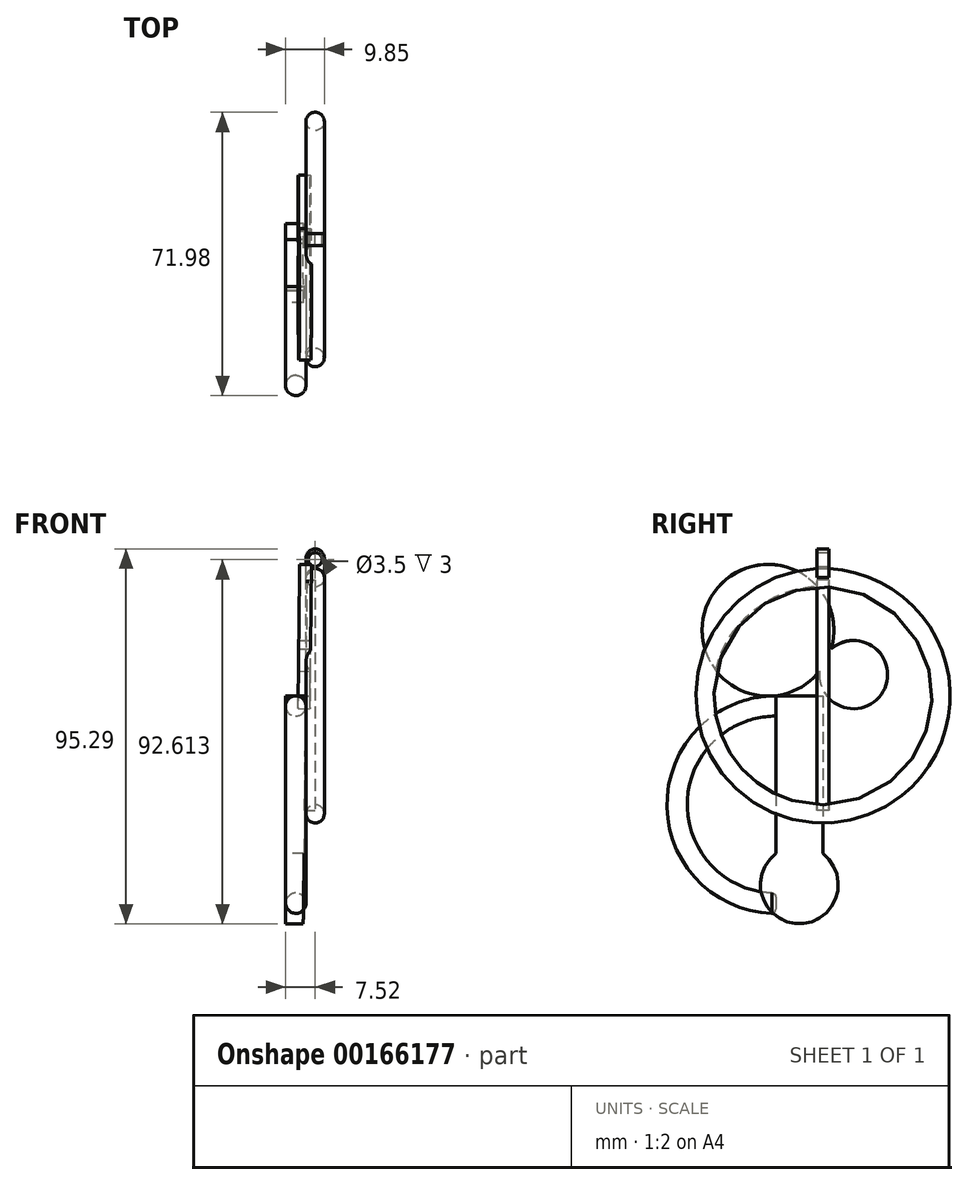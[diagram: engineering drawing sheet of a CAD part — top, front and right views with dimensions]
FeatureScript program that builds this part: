
annotation { "Feature Type Name" : "Feature", "Feature Type Description" : "" }
export const myFeature = defineFeature(function(context is Context, id is Id, definition is map)
    precondition{}
    {
        {
            var Q0;
            Q0=qCreatedBy(makeId("Front.planeOp"),FACE);
            var sketch = newSketch(context, id + "F0", { "sketchPlane" : qUnion([Q0])});
            skCircle(sketch, "E0", {"center": v(0, 30) * mm, "radius": 2.33 * mm});
            skLineSegment(sketch, "E1", {"start": v(-12.69, 0) * mm, "end": v(11.76, 0) * mm});
            skSolve(sketch);
        }
        {
            var Q0;
            Q0=makeQuery(id+"F0.imprint","IMPRINT",FACE,{"disambiguationData":[TD([[makeQuery(id+"F0.imprint","IMPRINT",EDGE,{"derivedFrom":sQuery(id+"F0.wireOp",EDGE,"E0")}),1.0]])]});
            var Q1;
            Q1=sQuery(id+"F0.wireOp",EDGE,"E1");
            revolve(context, id + "F1", {"entities" : qUnion([Q0]), "axis" : qUnion([Q1]), "revolveType" : RevolveType.FULL});
        }
        {
            var Q0;
            Q0=qCreatedBy(makeId("Front.planeOp"),FACE);
            var sketch = newSketch(context, id + "F2", { "sketchPlane" : qUnion([Q0])});
            skLineSegment(sketch, "E2", {"start": v(-2.33, -74.75) * mm, "end": v(-2.33, 74.75) * mm});
            skLineSegment(sketch, "E3.bottom", {"start": v(-2.33, 0) * mm, "end": v(-7.52, 0) * mm});
            skLineSegment(sketch, "E3.top", {"start": v(-2.8, -40) * mm, "end": v(-7.52, -40) * mm});
            skLineSegment(sketch, "E3.right", {"start": v(-7.52, 0) * mm, "end": v(-7.52, -40) * mm});
            skLineSegment(sketch, "E4", {"start": v(-2.33, 0) * mm, "end": v(-2.8, -40) * mm});
            skSolve(sketch);
        }
        {
            var Q0;
            Q0 = qSketchRegion(id + "F2", true);
            extrude(context, id + "F3", {"entities" : qUnion([Q0]), "operationType" : NewBodyOperationType.ADD, "depth" : 12 * mm});
        }
        {
            var Q0;
            Q0=makeQuery(id+"F3.opExtrude","SWEPT_FACE",FACE,{"disambiguationData":[OSD([sQuery(id+"F2.wireOp",EDGE,"E3.right")])]});
            var sketch = newSketch(context, id + "F4", { "sketchPlane" : qUnion([Q0])});
            skCircle(sketch, "E5", {"center": v(6, -48) * mm, "radius": 10 * mm});
            skSolve(sketch);
        }
        {
            var Q0;
            Q0 = qSketchRegion(id + "F4", true);
            var Q1;
            Q1=makeQuery(id+"F3.opExtrude","SWEPT_FACE",FACE,{"disambiguationData":[OSD([sQuery(id+"F2.wireOp",EDGE,"E4")])]});
            extrude(context, id + "F5", {"entities" : qUnion([Q0]), "operationType" : NewBodyOperationType.ADD, "endBound" : BoundingType.UP_TO_SURFACE, "oppositeDirection" : true, "endBoundEntityFace" : qUnion([Q1]), "depth" : 25 * mm});
        }
        {
            var Q0;
            Q0=makeQuery(id+"F3.opExtrude","CAP_FACE",FACE,{"disambiguationData":[OSD([sQuery(id+"F2.wireOp",EDGE,"E3.bottom"),sQuery(id+"F2.wireOp",EDGE,"E3.top"),sQuery(id+"F2.wireOp",EDGE,"E3.left"),sQuery(id+"F2.wireOp",EDGE,"E3.right")])],"isStart":false});
            var sketch = newSketch(context, id + "F6", { "sketchPlane" : qUnion([Q0])});
            skCircle(sketch, "E6", {"center": v(-4.94, -2.58) * mm, "radius": 2.58 * mm});
            skLineSegment(sketch, "E7", {"start": v(-50.54, -27.65) * mm, "end": v(51.9, -27.65) * mm});
            skSolve(sketch);
        }
        {
            var Q0;
            Q0 = qSketchRegion(id + "F6", true);
            var Q1;
            Q1=sQuery(id+"F6.wireOp",EDGE,"E7");
            revolve(context, id + "F7", {"entities" : qUnion([Q0]), "axis" : qUnion([Q1]), "revolveType" : RevolveType.ONE_DIRECTION, "angle" : 180 * degree});
        }
        {
            var Q0;
            {var subQ0=sQuery(id+"F2.wireOp",EDGE,"E4");Q0=makeQuery(id+"F5.boolean.opBoolean","MERGE",FACE,{"derivedFrom":[makeQuery(id+"F3.opExtrude","SWEPT_FACE",FACE,{"disambiguationData":[OSD([subQ0])]}),makeQuery(id+"F5.opExtrude","CAP_FACE",FACE,{"disambiguationData":[OSD([subQ0])],"isStart":false})]});}
            var sketch = newSketch(context, id + "F8", { "sketchPlane" : qUnion([Q0])});
            skCircle(sketch, "E8", {"center": v(-13.97, 16.64) * mm, "radius": 16.73 * mm});
            skCircle(sketch, "E9", {"center": v(7.75, 5.35) * mm, "radius": 8.67 * mm});
            skLineSegment(sketch, "E10.0.0", {"start": v(0, -0.1) * mm, "end": v(0, -40.09) * mm});
            skEllipticalArc(sketch, "E10.0.1", {});
            skLineSegment(sketch, "E10.0.2", {"start": v(-12, -40.09) * mm, "end": v(-12, -0.1) * mm});
            skLineSegment(sketch, "E10.0.3", {"start": v(-12, -0.1) * mm, "end": v(0, -0.1) * mm});
            const initialGuessF8  = {"E10.0.1": [-0.006, -0.058069764312871766, -1, 0, 0.01, 0.009999535525382323, 5.355890089177974, 4.068887871591405], "E10.0.1": [-0.006, -0.058069764312871766, -1, 0, 0.01, 0.009999535525382323, 5.355890089177974, 4.068887871591405]};
            skSetInitialGuess(sketch, initialGuessF8);
            skSolve(sketch);
        }
        {
            var Q0;
            {var subQ0=sQuery(id+"F8.wireOp",EDGE,"E9");var subQ1=sQuery(id+"F8.wireOp",EDGE,"E8");var subQ2=makeQuery(id+"F8.imprint","INTERSECT",VERTEX,{"disambiguationData":[OD(0.0)],"derivedFrom":[subQ1,subQ0]});Q0=makeQuery(id+"F8.imprint","IMPRINT",FACE,{"disambiguationData":[TD([[makeQuery(id+"F8.imprint","IMPRINT",EDGE,{"disambiguationData":[TD([[subQ2,1.0]])],"derivedFrom":subQ0}),-1.0]])]});}
            var Q1;
            {var subQ0=sQuery(id+"F8.wireOp",EDGE,"E9");var subQ1=sQuery(id+"F8.wireOp",EDGE,"E8");var subQ2=makeQuery(id+"F8.imprint","INTERSECT",VERTEX,{"disambiguationData":[OD(0.0)],"derivedFrom":[subQ1,subQ0]});Q1=makeQuery(id+"F8.imprint","IMPRINT",FACE,{"disambiguationData":[TD([[makeQuery(id+"F8.imprint","IMPRINT",EDGE,{"disambiguationData":[TD([[subQ2,-1.0]])],"derivedFrom":subQ1}),-1.0]])]});}
            var Q2;
            {var subQ0=sQuery(id+"F8.wireOp",EDGE,"E9");var subQ1=sQuery(id+"F8.wireOp",EDGE,"E8");var subQ2=makeQuery(id+"F8.imprint","INTERSECT",VERTEX,{"disambiguationData":[OD(0.0)],"derivedFrom":[subQ1,subQ0]});Q2=makeQuery(id+"F8.imprint","IMPRINT",FACE,{"disambiguationData":[TD([[makeQuery(id+"F8.imprint","IMPRINT",EDGE,{"disambiguationData":[TD([[subQ2,-1.0]])],"derivedFrom":subQ1}),1.0]])]});}
            extrude(context, id + "F9", {"entities" : qUnion([Q0, Q1, Q2]), "operationType" : NewBodyOperationType.ADD, "oppositeDirection" : true, "depth" : 2 * mm, "hasSecondDirection" : true, "secondDirectionOppositeDirection" : false, "secondDirectionDepth" : 1 * mm});
        }
        {
            var Q0;
            Q0=qCreatedBy(makeId("Right.planeOp"),FACE);
            var sketch = newSketch(context, id + "F10", { "sketchPlane" : qUnion([Q0])});
            skLineSegment(sketch, "E11.bottom", {"start": v(-1.5, 29.47) * mm, "end": v(1.5, 29.47) * mm});
            skLineSegment(sketch, "E11.top", {"start": v(-1.5, -29.15) * mm, "end": v(1.5, -29.15) * mm});
            skLineSegment(sketch, "E11.left", {"start": v(-1.5, 29.47) * mm, "end": v(-1.5, -29.15) * mm});
            skLineSegment(sketch, "E11.right", {"start": v(1.5, 29.47) * mm, "end": v(1.5, -29.15) * mm});
            skSolve(sketch);
        }
        {
            var Q0;
            Q0 = qSketchRegion(id + "F10", true);
            var Q1;
            {var subQ0=sQuery(id+"F2.wireOp",EDGE,"E4");Q1=makeQuery(id+"F5.boolean.opBoolean","MERGE",FACE,{"derivedFrom":[makeQuery(id+"F3.opExtrude","SWEPT_FACE",FACE,{"disambiguationData":[OSD([subQ0])]}),makeQuery(id+"F5.opExtrude","CAP_FACE",FACE,{"disambiguationData":[OSD([subQ0])],"isStart":false})]});}
            extrude(context, id + "F11", {"entities" : qUnion([Q0]), "endBound" : BoundingType.UP_TO_SURFACE, "oppositeDirection" : true, "endBoundEntityFace" : qUnion([Q1]), "depth" : 25 * mm});
        }
        {
            var Q0;
            Q0=qCreatedBy(makeId("Front.planeOp"),FACE);
            var sketch = newSketch(context, id + "F12", { "sketchPlane" : qUnion([Q0])});
            skArc(sketch, "E12", {"start": v(2.33, -30) * mm, "mid": v(0, -27.67) * mm, "end": v(-2.33, -30) * mm});
            skLineSegment(sketch, "E13", {"start": v(2.33, 30) * mm, "end": v(2.33, 34.96) * mm});
            skArc(sketch, "E14", {"start": v(2.33, 34.96) * mm, "mid": v(0, 37.29) * mm, "end": v(-2.33, 34.96) * mm});
            skLineSegment(sketch, "E15", {"start": v(-2.33, 30) * mm, "end": v(-2.33, 34.96) * mm});
            skCircle(sketch, "E16", {"center": v(0, 34.61) * mm, "radius": 1.75 * mm});
            skArc(sketch, "E17", {"start": v(2.33, 30) * mm, "mid": v(0, 32.33) * mm, "end": v(-2.33, 30) * mm});
            skSolve(sketch);
        }
        {
            var Q0;
            Q0=makeQuery(id+"F7.opRevolve","CAP_EDGE",EDGE,{"disambiguationData":[OSD([sQuery(id+"F6.wireOp",EDGE,"E6")])],"isStart":false});
            fillet(context, id + "F13", {"entities" : qUnion([Q0]), "radius" : 1 * mm, "tangentPropagation" : true, "allowEdgeOverflow" : false});
        }
        {
            var Q0;
            Q0=makeQuery(id+"F12.imprint","IMPRINT",FACE,{"disambiguationData":[TD([[makeQuery(id+"F12.imprint","IMPRINT",EDGE,{"derivedFrom":sQuery(id+"F12.wireOp",EDGE,"E13")}),1.0]])]});
            extrude(context, id + "F14", {"entities" : qUnion([Q0]), "operationType" : NewBodyOperationType.ADD, "endBound" : BoundingType.SYMMETRIC, "depth" : 3 * mm});
        }
    });
